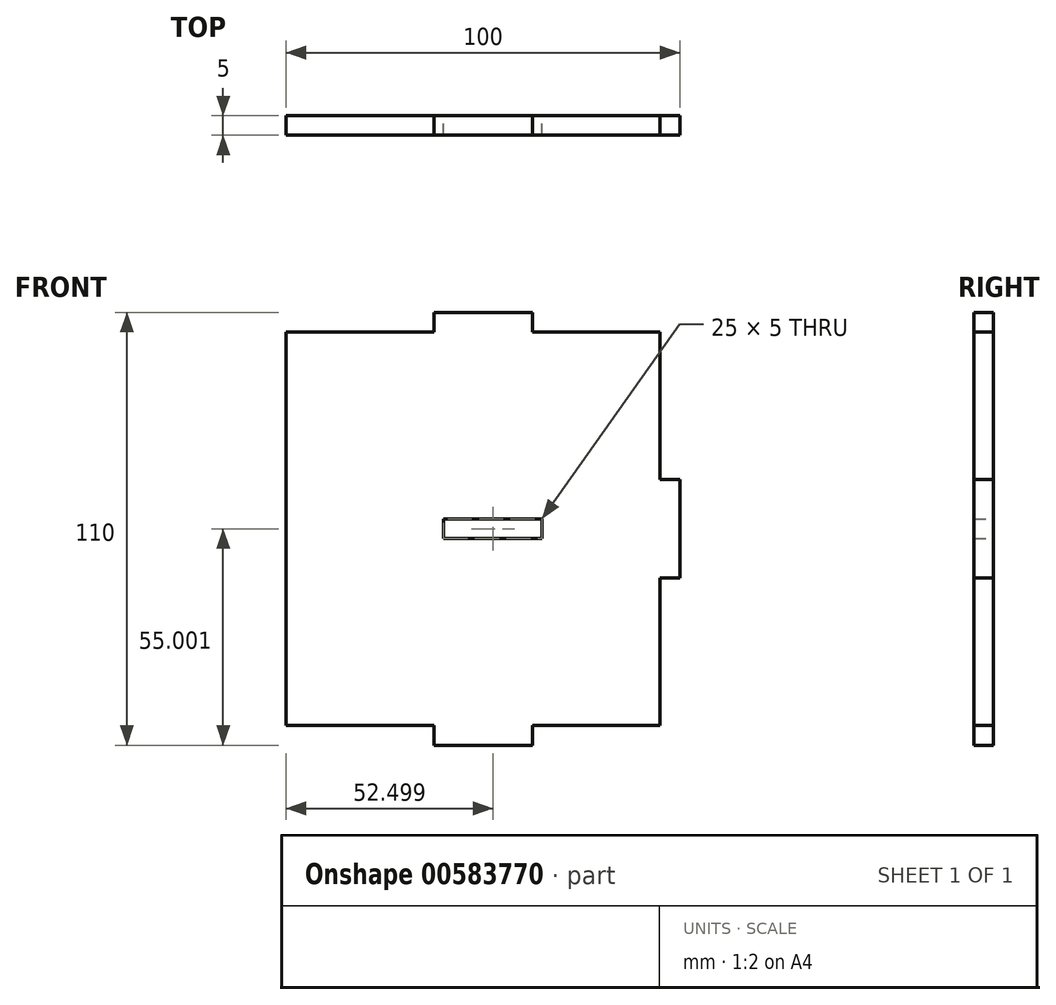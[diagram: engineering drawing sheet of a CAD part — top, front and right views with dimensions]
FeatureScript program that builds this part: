
annotation { "Feature Type Name" : "Feature", "Feature Type Description" : "" }
export const myFeature = defineFeature(function(context is Context, id is Id, definition is map)
    precondition{}
    {
        {
            var Q0;
            Q0=qCreatedBy(makeId("Front.planeOp"),FACE);
            var sketch = newSketch(context, id + "F0", { "sketchPlane" : qUnion([Q0])});
            skLineSegment(sketch, "E0", {"start": v(-73.48, 64.9) * mm, "end": v(-73.48, -35.1) * mm});
            skLineSegment(sketch, "E1", {"start": v(-73.48, -35.1) * mm, "end": v(-35.98, -35.1) * mm});
            skLineSegment(sketch, "E2", {"start": v(-35.98, -35.1) * mm, "end": v(-35.98, -40.1) * mm});
            skLineSegment(sketch, "E3", {"start": v(-35.98, -40.1) * mm, "end": v(-10.98, -40.1) * mm});
            skLineSegment(sketch, "E4", {"start": v(-10.98, -40.1) * mm, "end": v(-10.98, -35.1) * mm});
            skLineSegment(sketch, "E5", {"start": v(-10.98, -35.1) * mm, "end": v(21.52, -35.1) * mm});
            skLineSegment(sketch, "E6", {"start": v(21.52, -35.1) * mm, "end": v(21.52, 2.4) * mm});
            skLineSegment(sketch, "E7", {"start": v(21.52, 2.4) * mm, "end": v(26.52, 2.4) * mm});
            skLineSegment(sketch, "E8", {"start": v(26.52, 2.4) * mm, "end": v(26.52, 27.4) * mm});
            skLineSegment(sketch, "E9", {"start": v(26.52, 27.4) * mm, "end": v(21.52, 27.4) * mm});
            skLineSegment(sketch, "E10", {"start": v(21.52, 27.4) * mm, "end": v(21.52, 64.9) * mm});
            skLineSegment(sketch, "E11", {"start": v(-73.48, 64.9) * mm, "end": v(-35.98, 64.9) * mm});
            skLineSegment(sketch, "E12", {"start": v(-35.98, 64.9) * mm, "end": v(-35.98, 69.9) * mm});
            skLineSegment(sketch, "E13", {"start": v(-35.98, 69.9) * mm, "end": v(-10.98, 69.9) * mm});
            skLineSegment(sketch, "E14", {"start": v(-10.98, 64.9) * mm, "end": v(-10.98, 69.9) * mm});
            skLineSegment(sketch, "E15", {"start": v(21.52, 64.9) * mm, "end": v(-10.98, 64.9) * mm});
            skPoint(sketch, "E16.middle.positionSnap0", {"position": v(26.52, 14.9) * mm});
            skPoint(sketch, "E16.centerSnap0", {"position": v(26.52, 14.9) * mm});
            skLineSegment(sketch, "E17", {"start": v(26.52, 14.9) * mm, "end": v(-20.98, 14.9) * mm});
            skLineSegment(sketch, "E18.bottom", {"start": v(-33.48, 12.4) * mm, "end": v(-8.48, 12.4) * mm});
            skLineSegment(sketch, "E18.top", {"start": v(-33.48, 17.4) * mm, "end": v(-8.48, 17.4) * mm});
            skLineSegment(sketch, "E18.left", {"start": v(-33.48, 12.4) * mm, "end": v(-33.48, 17.4) * mm});
            skLineSegment(sketch, "E18.right", {"start": v(-8.48, 12.4) * mm, "end": v(-8.48, 17.4) * mm});
            skPoint(sketch, "E18.middle", {"position": v(-20.98, 14.9) * mm});
            skSolve(sketch);
        }
        {
            var Q0;
            Q0=makeQuery(id+"F0.imprint","IMPRINT",FACE,{"disambiguationData":[TD([[makeQuery(id+"F0.imprint","IMPRINT",EDGE,{"derivedFrom":sQuery(id+"F0.wireOp",EDGE,"E0")}),1.0]])]});
            extrude(context, id + "F1", {"entities" : qUnion([Q0]), "depth" : 5 * mm, "offsetDistance" : 25 * mm});
        }
    });
